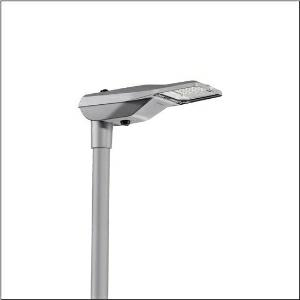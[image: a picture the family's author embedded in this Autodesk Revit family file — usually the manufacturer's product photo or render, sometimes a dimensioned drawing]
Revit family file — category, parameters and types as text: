
# Revit family: streetlight_sl_21_micro___p0_5a_5xe1v33t08db_2423
name_source: partatom
category: Lighting Fixtures
units: mm (PartAtom-declared; Revit-internal decimal feet)

## family parameters
Cut with Voids When Loaded = No
Host = Face
Light Source = No
Part Type = Normal
Room Calculation Point = No
Round Connector Dimension = Use Diameter
Shared = No

## types (1)
- --- (1 x LED, 4940 lm, 39.1 W, 3000K)
    Apparent Load = 39 VA
    CIE Flux Codes = 37 73 96 100 100
    Color Rendering = 70
    Color Temperature = 3000K
    Default Elevation = 1800 mm
    Description = Streetlight SL 21 micro, mast luminaire, primary light control with lens, of PMMA, primary optical cover: cover, of toughened safety glass, transparent, light distribution: P0.5a, light emission: direct distribution, primary light characteristic: asymmetric, installation type: post-top, side-entry, LED, High Power LED, rated luminous flux: 4.940lm, luminous efficacy: 126lm/W, light colour: 730, colour temperature: 3000K, control gear: D4i, control: pre-setting: logarithmic dimming characteristic, flexible luminous flux parameterisation, time-dependent luminous flux control, constant luminous flux control, overheat protection, mains connection: 220..240V, AC, 50/60Hz, start of lifetime: 39W, end of service life: 41W, reduction: 18W, luminaire housing, of diecast aluminium, powder-coated, Siteco® metallic grey (DB 702S), corrosivity category C5 mid according to DIN EN ISO 12944, multi-level sealing system, sealing non-destructively replaceable, inclination adjustable: 0°, 5°, 10°, 15°, please order mast flange separately, length: 528mm, width: 235mm, height: 110mm, mast flange for spigot size: 42mm (side-entry): 5XC10008XM4, 60/48mm (side-entry/post-top): 5XC10108XM2, 76/60mm (side-entry/post-top): 5XC10108XM1, Smart Interface below and above, protection rating (complete): IP66, insulation class (complete): insulation class II (safety insulation), certification: CE, ENEC, ENEC+, VDE, impact resistance: IK10, permissible operating ambient temperature for outdoor applications: -40..+50°C, standard-compliant lighting for roads and squares, packaging unit: 1 piece

Light Distribution: P0.5a
    Height = 110 mm
    Lamp = 1 x LED
    Lamp Light Flux = 4940 lm
    Lamp Power = 39.1 W
    Lamp count = 1
    Length = 528 mm
    Luminous efficacy = 126 lm/W
    Manufacturer = Siteco
    ModVariant = No
    Model = 5XE1V33T08DB
    Number of Poles = 1
    OnlyDefault = Yes
    Power Factor = 1
    Product Name = Streetlight SL 21 micro | P0.5a
    Product group = mast luminaire | pylon top
    ProductGroupID = 6100
    Protection Class = Protection class II
    Protection Degree = IP 66
    RLX_Detail_Level = 1
    RLX_Emergency_Light_Flux = 0 lm
    RLX_Emergency_Type = 0
    RLX_Emergency_Type_DB = No
    RlxData = <blob elided: 97705 chars, md5=fbaaa3d1>
    Socket = socket
    Standby Power = 0 W
    System Light Flux = 4940 lm
    System Power = 39 W
    Type Comments = factory setting: luminous flux: 100 % | dim-lin: 254 | 765 mA
    Type Image = l_1007239.jpg
    URL = http://relux.com
    VarID = @adj_070066
    Voltage = 0 V
    Weight = 0.00 kg
    Width = 235 mm

## geometry (parser evidence)
native form markers: Blend x4, Sweep x10
no freeform markers — native parametric forms only
